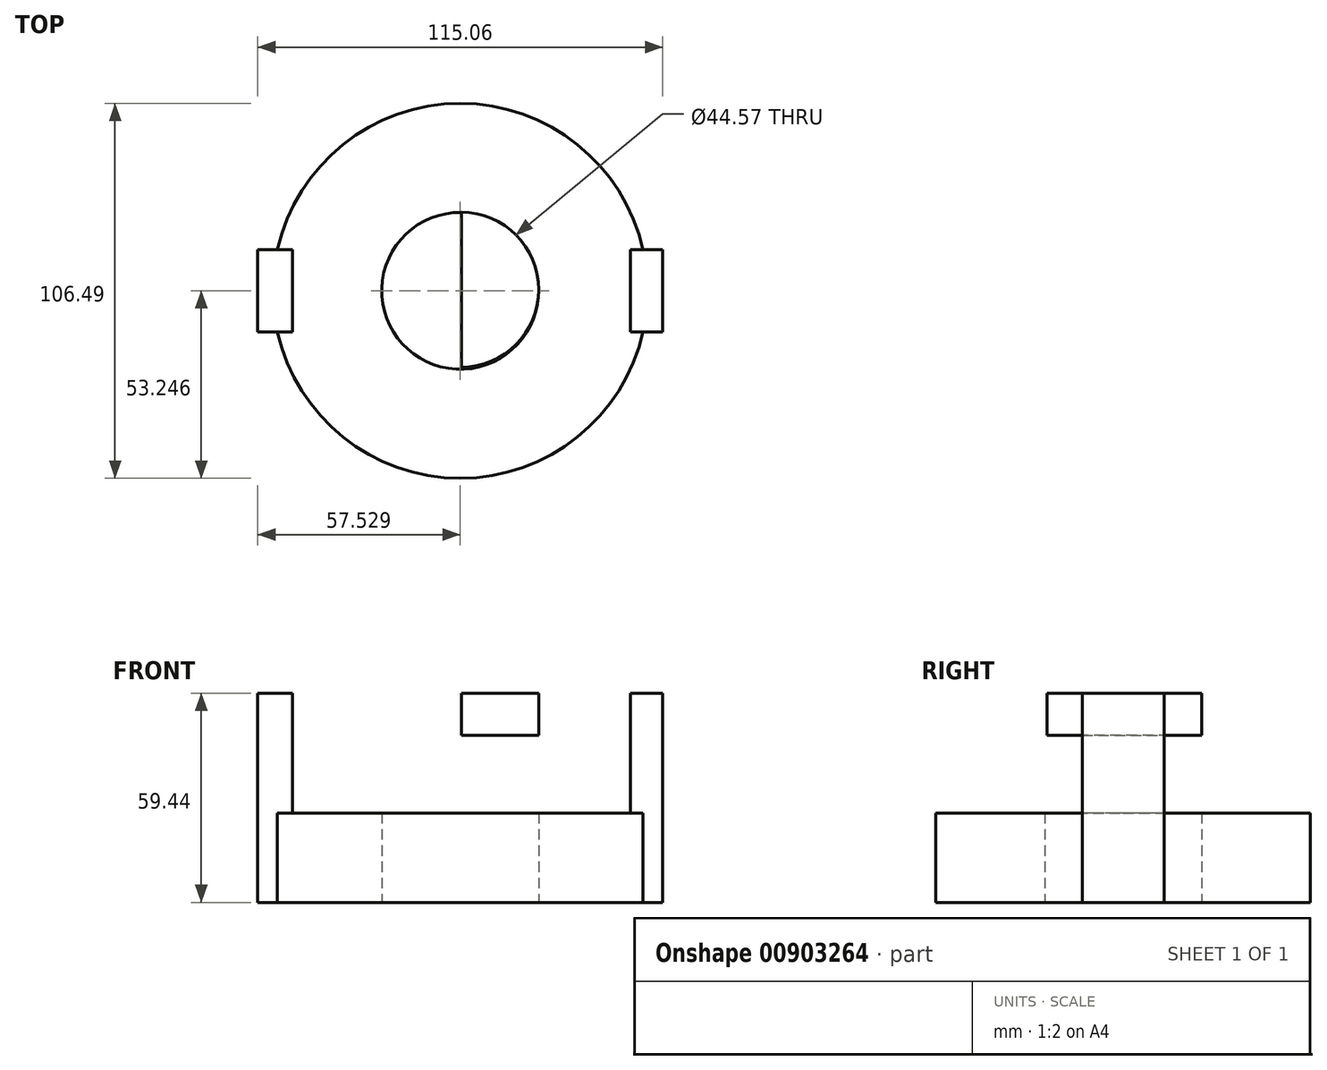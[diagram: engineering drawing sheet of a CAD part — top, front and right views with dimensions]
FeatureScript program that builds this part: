
annotation { "Feature Type Name" : "Feature", "Feature Type Description" : "" }
export const myFeature = defineFeature(function(context is Context, id is Id, definition is map)
    precondition{}
    {
        {
            var Q0;
            Q0=qCreatedBy(makeId("Top.planeOp"),FACE);
            var sketch = newSketch(context, id + "F0", { "sketchPlane" : qUnion([Q0])});
            skCircle(sketch, "E0", {"center": v(-25.17, 0.86) * mm, "radius": 22.28 * mm});
            skCircle(sketch, "E1", {"center": v(-25.17, 0.86) * mm, "radius": 74.55 * mm});
            skLineSegment(sketch, "E2", {"start": v(-25.17, 0.86) * mm, "end": v(-99.72, 0.86) * mm});
            skLineSegment(sketch, "E3", {"start": v(-99.72, 0.86) * mm, "end": v(49.38, 0.86) * mm});
            skLineSegment(sketch, "E4.bottom", {"start": v(-82.7, 12.5) * mm, "end": v(-67.98, 12.5) * mm});
            skLineSegment(sketch, "E4.top", {"start": v(-82.7, 0.86) * mm, "end": v(-67.98, 0.86) * mm});
            skLineSegment(sketch, "E4.left", {"start": v(-82.7, 12.5) * mm, "end": v(-82.7, 0.86) * mm});
            skLineSegment(sketch, "E4.right", {"start": v(-67.98, 12.5) * mm, "end": v(-67.98, 0.86) * mm});
            skLineSegment(sketch, "E5", {"start": v(-99.72, 0.86) * mm, "end": v(49.38, 0.86) * mm, "construction": true});
            skLineSegment(sketch, "E6", {"start": v(-25.17, 75.4) * mm, "end": v(-25.17, -73.7) * mm, "construction": true});
            skLineSegment(sketch, "E7.MirrorCS", {"start": v(-67.98, -10.79) * mm, "end": v(-67.98, 0.86) * mm});
            skLineSegment(sketch, "E8.MirrorCS", {"start": v(-82.7, -10.79) * mm, "end": v(-67.98, -10.79) * mm});
            skLineSegment(sketch, "E9.MirrorCS", {"start": v(-82.7, -10.79) * mm, "end": v(-82.7, 0.86) * mm});
            skLineSegment(sketch, "E10.MirrorCS", {"start": v(17.64, 12.5) * mm, "end": v(17.64, 0.86) * mm});
            skLineSegment(sketch, "E11.MirrorCS", {"start": v(17.64, -10.79) * mm, "end": v(17.64, 0.86) * mm});
            skLineSegment(sketch, "E12.MirrorCS", {"start": v(32.36, -10.79) * mm, "end": v(17.64, -10.79) * mm});
            skLineSegment(sketch, "E13.MirrorCS", {"start": v(32.36, -10.79) * mm, "end": v(32.36, 0.86) * mm});
            skLineSegment(sketch, "E14.MirrorCS", {"start": v(32.36, 12.5) * mm, "end": v(32.36, 0.86) * mm});
            skLineSegment(sketch, "E15.MirrorCS", {"start": v(32.36, 12.5) * mm, "end": v(17.64, 12.5) * mm});
            skCircle(sketch, "E16", {"center": v(-25.17, 0.86) * mm, "radius": 53.24 * mm});
            skSolve(sketch);
        }
        {
            var Q0;
            {var subQ0=sQuery(id+"F0.wireOp",EDGE,"E7.MirrorCS");Q0=makeQuery(id+"F0.imprint","IMPRINT",FACE,{"disambiguationData":[TD([[makeQuery(id+"F0.imprint","IMPRINT",EDGE,{"derivedFrom":subQ0}),-1.0]])]});}
            var Q1;
            {var subQ3=sQuery(id+"F0.wireOp",EDGE,"E4.right");Q1=makeQuery(id+"F0.imprint","IMPRINT",FACE,{"disambiguationData":[TD([[makeQuery(id+"F0.imprint","IMPRINT",EDGE,{"derivedFrom":subQ3}),1.0]])]});}
            var Q2;
            {var subQ0=sQuery(id+"F0.wireOp",EDGE,"E7.MirrorCS");Q2=makeQuery(id+"F0.imprint","IMPRINT",FACE,{"disambiguationData":[TD([[makeQuery(id+"F0.imprint","IMPRINT",EDGE,{"derivedFrom":subQ0}),1.0]])]});}
            var Q3;
            {var subQ0=sQuery(id+"F0.wireOp",EDGE,"E4.right");Q3=makeQuery(id+"F0.imprint","IMPRINT",FACE,{"disambiguationData":[TD([[makeQuery(id+"F0.imprint","IMPRINT",EDGE,{"derivedFrom":subQ0}),-1.0]])]});}
            var Q4;
            {var subQ0=sQuery(id+"F0.wireOp",EDGE,"E4.left");Q4=makeQuery(id+"F0.imprint","IMPRINT",FACE,{"disambiguationData":[TD([[makeQuery(id+"F0.imprint","IMPRINT",EDGE,{"derivedFrom":subQ0}),1.0]])]});}
            var Q5;
            {var subQ0=sQuery(id+"F0.wireOp",EDGE,"E9.MirrorCS");Q5=makeQuery(id+"F0.imprint","IMPRINT",FACE,{"disambiguationData":[TD([[makeQuery(id+"F0.imprint","IMPRINT",EDGE,{"derivedFrom":subQ0}),-1.0]])]});}
            var Q6;
            {var subQ0=sQuery(id+"F0.wireOp",EDGE,"E14.MirrorCS");Q6=makeQuery(id+"F0.imprint","IMPRINT",FACE,{"disambiguationData":[TD([[makeQuery(id+"F0.imprint","IMPRINT",EDGE,{"derivedFrom":subQ0}),-1.0]])]});}
            var Q7;
            {var subQ0=sQuery(id+"F0.wireOp",EDGE,"E13.MirrorCS");Q7=makeQuery(id+"F0.imprint","IMPRINT",FACE,{"disambiguationData":[TD([[makeQuery(id+"F0.imprint","IMPRINT",EDGE,{"derivedFrom":subQ0}),1.0]])]});}
            var Q8;
            {var subQ0=sQuery(id+"F0.wireOp",EDGE,"E11.MirrorCS");Q8=makeQuery(id+"F0.imprint","IMPRINT",FACE,{"disambiguationData":[TD([[makeQuery(id+"F0.imprint","IMPRINT",EDGE,{"derivedFrom":subQ0}),-1.0]])]});}
            var Q9;
            {var subQ0=sQuery(id+"F0.wireOp",EDGE,"E10.MirrorCS");Q9=makeQuery(id+"F0.imprint","IMPRINT",FACE,{"disambiguationData":[TD([[makeQuery(id+"F0.imprint","IMPRINT",EDGE,{"derivedFrom":subQ0}),1.0]])]});}
            extrude(context, id + "F1", {"entities" : qUnion([Q0, Q1, Q2, Q3, Q4, Q5, Q6, Q7, Q8, Q9]), "depth" : 25.4 * mm, "offsetDistance" : 25.4 * mm});
        }
        {
            var Q0;
            Q0=makeQuery(id+"F1.opExtrude","CAP_FACE",FACE,{"disambiguationData":[OSD([sQuery(id+"F0.wireOp",EDGE,"E0"),sQuery(id+"F0.wireOp",EDGE,"E4.bottom"),sQuery(id+"F0.wireOp",EDGE,"E4.left"),sQuery(id+"F0.wireOp",EDGE,"E8.MirrorCS"),sQuery(id+"F0.wireOp",EDGE,"E9.MirrorCS"),sQuery(id+"F0.wireOp",EDGE,"E12.MirrorCS"),sQuery(id+"F0.wireOp",EDGE,"E13.MirrorCS"),sQuery(id+"F0.wireOp",EDGE,"E14.MirrorCS"),sQuery(id+"F0.wireOp",EDGE,"E15.MirrorCS"),sQuery(id+"F0.wireOp",EDGE,"E16")])],"isStart":false});
            var sketch = newSketch(context, id + "F2", { "sketchPlane" : qUnion([Q0])});
            skLineSegment(sketch, "E17.bottom", {"start": v(-82.7, 12.5) * mm, "end": v(-72.79, 12.5) * mm});
            skLineSegment(sketch, "E17.top", {"start": v(-82.7, -10.79) * mm, "end": v(-72.79, -10.79) * mm});
            skLineSegment(sketch, "E17.left", {"start": v(-82.7, 12.5) * mm, "end": v(-82.7, -10.79) * mm});
            skLineSegment(sketch, "E17.right", {"start": v(-72.79, 12.5) * mm, "end": v(-72.79, -10.79) * mm});
            skLineSegment(sketch, "E18.bottom", {"start": v(32.36, 12.5) * mm, "end": v(23.2, 12.5) * mm});
            skLineSegment(sketch, "E18.top", {"start": v(32.36, -10.79) * mm, "end": v(23.2, -10.79) * mm});
            skLineSegment(sketch, "E18.left", {"start": v(32.36, 12.5) * mm, "end": v(32.36, -10.79) * mm});
            skLineSegment(sketch, "E18.right", {"start": v(23.2, 12.5) * mm, "end": v(23.2, -10.79) * mm});
            skSolve(sketch);
        }
        {
            var Q0;
            {var subQ4=sQuery(id+"F2.wireOp",EDGE,"E17.left");Q0=makeQuery(id+"F2.imprint","IMPRINT",FACE,{"disambiguationData":[TD([[makeQuery(id+"F2.imprint","IMPRINT",EDGE,{"derivedFrom":subQ4}),1.0]])]});}
            var Q1;
            {var subQ4=sQuery(id+"F2.wireOp",EDGE,"E18.left");Q1=makeQuery(id+"F2.imprint","IMPRINT",FACE,{"disambiguationData":[TD([[makeQuery(id+"F2.imprint","IMPRINT",EDGE,{"derivedFrom":subQ4}),-1.0]])]});}
            extrude(context, id + "F3", {"entities" : qUnion([Q0, Q1]), "operationType" : NewBodyOperationType.ADD, "depth" : 34.04 * mm, "offsetDistance" : 25.4 * mm});
        }
        {
            var Q0;
            Q0=makeQuery(id+"F3.opExtrude","CAP_FACE",FACE,{"disambiguationData":[OSD([sQuery(id+"F2.wireOp",EDGE,"E17.bottom"),sQuery(id+"F2.wireOp",EDGE,"E17.top"),sQuery(id+"F2.wireOp",EDGE,"E17.left"),sQuery(id+"F2.wireOp",EDGE,"E17.right")])],"isStart":false});
            var sketch = newSketch(context, id + "F4", { "sketchPlane" : qUnion([Q0])});
            skLineSegment(sketch, "E19", {"start": v(-82.7, 0.86) * mm, "end": v(36.1, 0.86) * mm});
            skLineSegment(sketch, "E20", {"start": v(-24.86, 54.55) * mm, "end": v(-24.86, -52.21) * mm});
            skCircle(sketch, "E21", {"center": v(-24.86, 1.17) * mm, "radius": 56.02 * mm});
            skCircle(sketch, "E22", {"center": v(-24.86, 1.17) * mm, "radius": 22 * mm});
            skSolve(sketch);
        }
        {
            var Q0;
            {var subQ0=sQuery(id+"F4.wireOp",EDGE,"E22");var subQ2=sQuery(id+"F4.wireOp",EDGE,"E19");var subQ3=makeQuery(id+"F4.imprint","INTERSECT",VERTEX,{"disambiguationData":[OD(0.0)],"derivedFrom":[subQ2,subQ0]});Q0=makeQuery(id+"F4.imprint","IMPRINT",FACE,{"disambiguationData":[TD([[makeQuery(id+"F4.imprint","IMPRINT",EDGE,{"disambiguationData":[TD([[subQ3,1.0]])],"derivedFrom":subQ2}),-1.0]])]});}
            var Q1;
            {var subQ1=sQuery(id+"F4.wireOp",EDGE,"E19");var subQ8=sQuery(id+"F4.wireOp",EDGE,"E22");var subQ11=makeQuery(id+"F4.imprint","INTERSECT",VERTEX,{"disambiguationData":[OD(0.0)],"derivedFrom":[subQ1,subQ8]});Q1=makeQuery(id+"F4.imprint","IMPRINT",FACE,{"disambiguationData":[TD([[makeQuery(id+"F4.imprint","IMPRINT",EDGE,{"disambiguationData":[TD([[subQ11,1.0]])],"derivedFrom":subQ1}),1.0]])]});}
            extrude(context, id + "F5", {"entities" : qUnion([Q0, Q1]), "operationType" : NewBodyOperationType.ADD, "oppositeDirection" : true, "depth" : 11.94 * mm, "offsetDistance" : 25.4 * mm});
        }
    });
